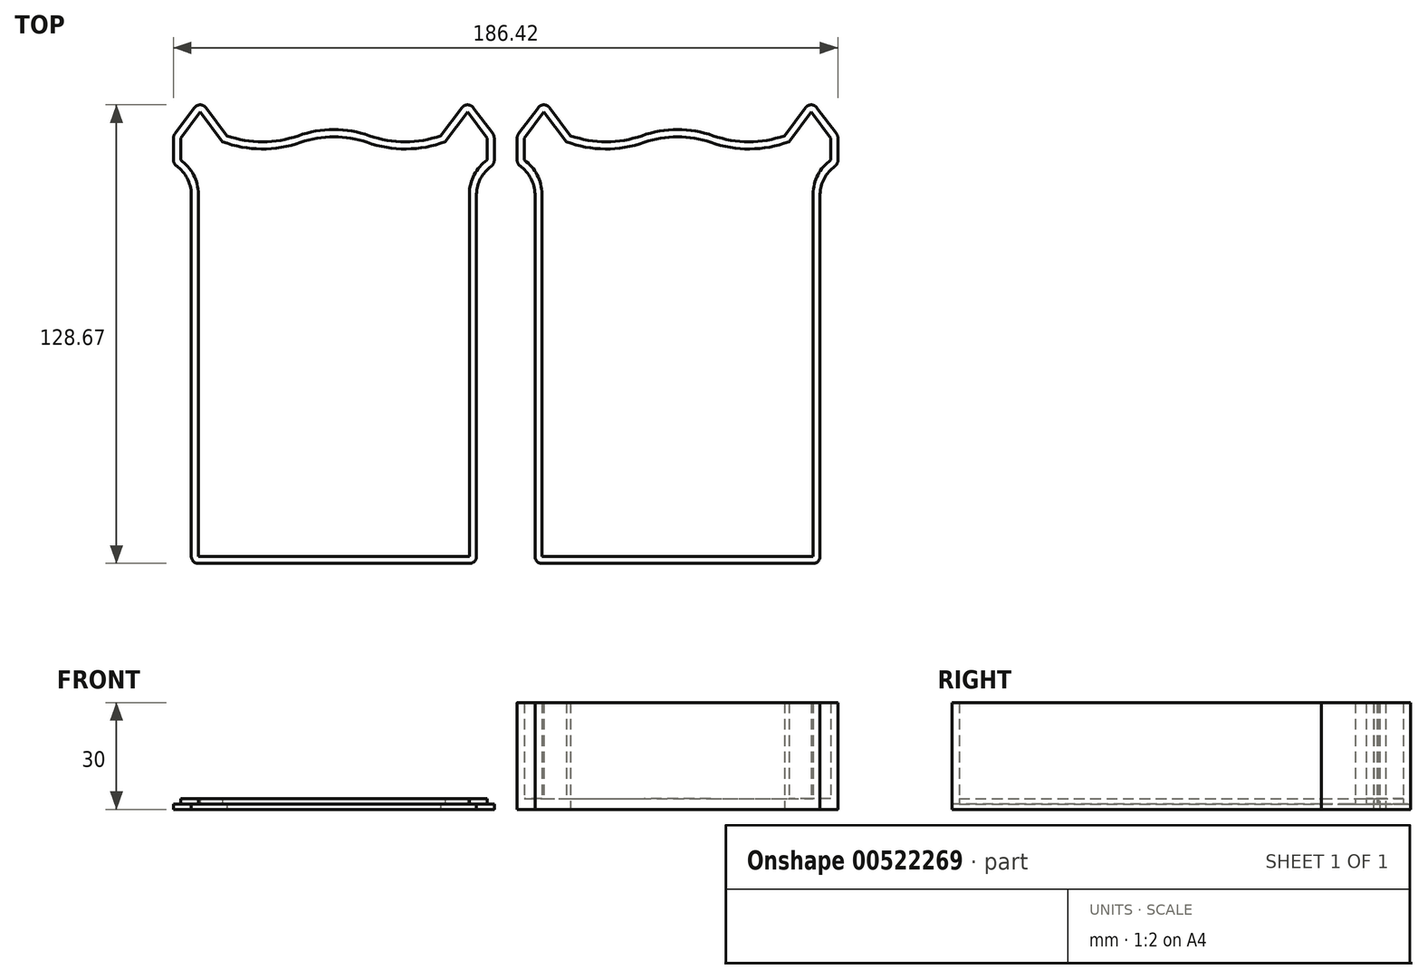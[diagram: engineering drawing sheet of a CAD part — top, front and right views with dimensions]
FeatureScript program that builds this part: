
annotation { "Feature Type Name" : "Feature", "Feature Type Description" : "" }
export const myFeature = defineFeature(function(context is Context, id is Id, definition is map)
    precondition{}
    {
        {
            var Q0;
            Q0=qCreatedBy(makeId("Top.planeOp"),FACE);
            var sketch = newSketch(context, id + "F0", { "sketchPlane" : qUnion([Q0])});
            skLineSegment(sketch, "E0", {"start": v(2, 0) * mm, "end": v(78, 0) * mm});
            skLineSegment(sketch, "E1", {"start": v(0, 2) * mm, "end": v(0, 103.64) * mm});
            skLineSegment(sketch, "E2", {"start": v(80, 103.6) * mm, "end": v(80, 2) * mm});
            skPoint(sketch, "E3", {"position": v(80, 110) * mm});
            skPoint(sketch, "E4", {"position": v(40, 120) * mm});
            skPoint(sketch, "E5", {"position": v(10, 120) * mm});
            skPoint(sketch, "E6", {"position": v(30, 120) * mm});
            skPoint(sketch, "E7", {"position": v(50, 120) * mm});
            skArc(sketch, "E8", {"start": v(10, 120) * mm, "mid": v(20, 118.28) * mm, "end": v(30, 120) * mm});
            skArc(sketch, "E9", {"start": v(50, 120) * mm, "mid": v(40, 121.72) * mm, "end": v(30, 120) * mm});
            skArc(sketch, "E10", {"start": v(50, 120) * mm, "mid": v(60, 118.28) * mm, "end": v(70, 120) * mm});
            skPoint(sketch, "E11", {"position": v(20, 130.8) * mm});
            skPoint(sketch, "E11.positionSnap0", {"position": v(20, 118.28) * mm});
            skLineSegment(sketch, "E12", {"start": v(-5, 113.15) * mm, "end": v(-5, 119.33) * mm});
            skLineSegment(sketch, "E13", {"start": v(85, 113.09) * mm, "end": v(85, 119.33) * mm});
            skLineSegment(sketch, "E14", {"start": v(-4.6, 120.53) * mm, "end": v(0.9, 127.87) * mm});
            skLineSegment(sketch, "E15", {"start": v(4.1, 127.87) * mm, "end": v(10, 120) * mm});
            skPoint(sketch, "E16", {"position": v(-5, 120) * mm});
            skPoint(sketch, "E17", {"position": v(2.5, 120) * mm});
            skPoint(sketch, "E18.visualSharp", {"position": v(2.5, 130) * mm});
            skArc(sketch, "E18.filletArc", {"start": v(4.1, 127.87) * mm, "mid": v(2.5, 128.67) * mm, "end": v(0.9, 127.87) * mm});
            skPoint(sketch, "E19.endSnap0", {"position": v(40, 110) * mm});
            skLineSegment(sketch, "E20.MirrorCS", {"start": v(75.9, 127.87) * mm, "end": v(70, 120) * mm});
            skLineSegment(sketch, "E21.MirrorCS", {"start": v(84.6, 120.53) * mm, "end": v(79.1, 127.87) * mm});
            skArc(sketch, "E22.MirrorCS", {"start": v(75.9, 127.87) * mm, "mid": v(77.5, 128.67) * mm, "end": v(79.1, 127.87) * mm});
            skPoint(sketch, "E23.visualSharp", {"position": v(85, 110) * mm});
            skPoint(sketch, "E24.visualSharp", {"position": v(-5, 110) * mm});
            skArc(sketch, "E25", {"start": v(0, 103.64) * mm, "mid": v(-1.16, 108.08) * mm, "end": v(-4.17, 111.53) * mm});
            skPoint(sketch, "E26.orphan", {"position": v(0, 110) * mm});
            skPoint(sketch, "E27.visualSharp", {"position": v(-5, 112.07) * mm});
            skArc(sketch, "E27.filletArc", {"start": v(-5, 113.15) * mm, "mid": v(-4.78, 112.24) * mm, "end": v(-4.17, 111.53) * mm});
            skArc(sketch, "E28.filletArc", {"start": v(-4.6, 120.53) * mm, "mid": v(-4.9, 119.97) * mm, "end": v(-5, 119.33) * mm});
            skArc(sketch, "E29.MirrorCS", {"start": v(80, 103.6) * mm, "mid": v(81.16, 108.02) * mm, "end": v(84.17, 111.46) * mm});
            skArc(sketch, "E30.MirrorCS", {"start": v(85, 113.09) * mm, "mid": v(84.78, 112.17) * mm, "end": v(84.17, 111.46) * mm});
            skPoint(sketch, "E31.visualSharp", {"position": v(85, 120) * mm});
            skArc(sketch, "E31.filletArc", {"start": v(85, 119.33) * mm, "mid": v(84.9, 119.97) * mm, "end": v(84.6, 120.53) * mm});
            skArc(sketch, "E32.0", {"start": v(8.76, 118.32) * mm, "mid": v(19.7, 116.29) * mm, "end": v(30.67, 118.11) * mm});
            skLineSegment(sketch, "E32.1", {"start": v(2.5, 126.67) * mm, "end": v(8.76, 118.32) * mm});
            skLineSegment(sketch, "E32.2", {"start": v(2, 2) * mm, "end": v(2, 103.67) * mm});
            skArc(sketch, "E32.3", {"start": v(2, 103.67) * mm, "mid": v(0.62, 109) * mm, "end": v(-3, 113.15) * mm});
            skLineSegment(sketch, "E32.4", {"start": v(-3, 113.15) * mm, "end": v(-3, 119.33) * mm});
            skLineSegment(sketch, "E32.5", {"start": v(-3, 119.33) * mm, "end": v(2.5, 126.67) * mm});
            skArc(sketch, "E33.MirrorCS", {"start": v(71.24, 118.32) * mm, "mid": v(60.3, 116.29) * mm, "end": v(49.33, 118.11) * mm});
            skLineSegment(sketch, "E34.MirrorCS", {"start": v(77.5, 126.67) * mm, "end": v(71.24, 118.32) * mm});
            skLineSegment(sketch, "E35.MirrorCS", {"start": v(83, 119.33) * mm, "end": v(77.5, 126.67) * mm});
            skLineSegment(sketch, "E36.MirrorCS", {"start": v(83, 113.15) * mm, "end": v(83, 119.33) * mm});
            skArc(sketch, "E37.MirrorCS", {"start": v(78, 103.67) * mm, "mid": v(79.38, 109) * mm, "end": v(83, 113.15) * mm});
            skArc(sketch, "E38.0", {"start": v(49.33, 118.11) * mm, "mid": v(40, 119.72) * mm, "end": v(30.67, 118.11) * mm});
            skLineSegment(sketch, "E39.0", {"start": v(2, 2) * mm, "end": v(78, 2) * mm});
            skLineSegment(sketch, "E39.1", {"start": v(78, 103.6) * mm, "end": v(78, 2) * mm});
            skLineSegment(sketch, "E40", {"start": v(78, 103.6) * mm, "end": v(78, 103.67) * mm});
            skPoint(sketch, "E41", {"position": v(0, 0) * mm});
            skPoint(sketch, "E42", {"position": v(2, 2) * mm});
            skArc(sketch, "E43.filletArc", {"start": v(0, 2) * mm, "mid": v(0.59, 0.59) * mm, "end": v(2, 0) * mm});
            skPoint(sketch, "E44.visualSharp", {"position": v(80, 0) * mm});
            skArc(sketch, "E44.filletArc", {"start": v(78, 0) * mm, "mid": v(79.41, 0.59) * mm, "end": v(80, 2) * mm});
            skSolve(sketch);
        }
        {
            var Q0;
            Q0=makeQuery(id+"F0.imprint","IMPRINT",FACE,{"disambiguationData":[TD([[makeQuery(id+"F0.imprint","IMPRINT",EDGE,{"derivedFrom":sQuery(id+"F0.wireOp",EDGE,"E0")}),1.0]])]});
            extrude(context, id + "F1", {"entities" : qUnion([Q0]), "depth" : 30 * mm, "offsetDistance" : 25 * mm});
        }
        {
            var Q0;
            Q0=makeQuery(id+"F0.imprint","IMPRINT",FACE,{"disambiguationData":[TD([[makeQuery(id+"F0.imprint","IMPRINT",EDGE,{"derivedFrom":sQuery(id+"F0.wireOp",EDGE,"E32.0")}),-1.0]])]});
            extrude(context, id + "F2", {"entities" : qUnion([Q0]), "operationType" : NewBodyOperationType.ADD, "depth" : 3 * mm, "offsetDistance" : 25 * mm});
        }
        {
            var Q0;
            Q0=qCreatedBy(makeId("Top.planeOp"),FACE);
            var sketch = newSketch(context, id + "F3", { "sketchPlane" : qUnion([Q0])});
            skLineSegment(sketch, "E45", {"start": v(-94.42, 0) * mm, "end": v(-18.42, 0) * mm});
            skLineSegment(sketch, "E46", {"start": v(-96.42, 2) * mm, "end": v(-96.42, 103.64) * mm});
            skLineSegment(sketch, "E47", {"start": v(-16.42, 103.6) * mm, "end": v(-16.42, 2) * mm});
            skPoint(sketch, "E48", {"position": v(-16.42, 110) * mm});
            skPoint(sketch, "E49", {"position": v(-56.42, 120) * mm});
            skPoint(sketch, "E50", {"position": v(-86.42, 120) * mm});
            skPoint(sketch, "E51", {"position": v(-66.42, 120) * mm});
            skPoint(sketch, "E52", {"position": v(-46.42, 120) * mm});
            skArc(sketch, "E53", {"start": v(-86.42, 120) * mm, "mid": v(-76.42, 118.28) * mm, "end": v(-66.42, 120) * mm});
            skArc(sketch, "E54", {"start": v(-46.42, 120) * mm, "mid": v(-56.42, 121.72) * mm, "end": v(-66.42, 120) * mm});
            skArc(sketch, "E55", {"start": v(-46.42, 120) * mm, "mid": v(-36.42, 118.28) * mm, "end": v(-26.42, 120) * mm});
            skPoint(sketch, "E56", {"position": v(-76.42, 130.8) * mm});
            skPoint(sketch, "E56.positionSnap0", {"position": v(-76.42, 118.28) * mm});
            skLineSegment(sketch, "E57", {"start": v(-101.42, 113.15) * mm, "end": v(-101.42, 119.33) * mm});
            skLineSegment(sketch, "E58", {"start": v(-11.42, 113.09) * mm, "end": v(-11.42, 119.33) * mm});
            skLineSegment(sketch, "E59", {"start": v(-101.02, 120.53) * mm, "end": v(-95.52, 127.87) * mm});
            skLineSegment(sketch, "E60", {"start": v(-92.32, 127.87) * mm, "end": v(-86.42, 120) * mm});
            skPoint(sketch, "E61", {"position": v(-101.42, 120) * mm});
            skPoint(sketch, "E62", {"position": v(-93.92, 120) * mm});
            skPoint(sketch, "E63.visualSharp", {"position": v(-93.92, 130) * mm});
            skArc(sketch, "E63.filletArc", {"start": v(-92.32, 127.87) * mm, "mid": v(-93.92, 128.67) * mm, "end": v(-95.52, 127.87) * mm});
            skPoint(sketch, "E64.endSnap0", {"position": v(-56.42, 110) * mm});
            skLineSegment(sketch, "E65.MirrorCS", {"start": v(-20.52, 127.87) * mm, "end": v(-26.42, 120) * mm});
            skLineSegment(sketch, "E66.MirrorCS", {"start": v(-11.82, 120.53) * mm, "end": v(-17.32, 127.87) * mm});
            skArc(sketch, "E67.MirrorCS", {"start": v(-20.52, 127.87) * mm, "mid": v(-18.92, 128.67) * mm, "end": v(-17.32, 127.87) * mm});
            skPoint(sketch, "E68.visualSharp", {"position": v(-11.42, 110) * mm});
            skPoint(sketch, "E69.visualSharp", {"position": v(-101.42, 110) * mm});
            skArc(sketch, "E70", {"start": v(-96.42, 103.64) * mm, "mid": v(-97.57, 108.08) * mm, "end": v(-100.59, 111.53) * mm});
            skPoint(sketch, "E71.orphan", {"position": v(-96.42, 110) * mm});
            skPoint(sketch, "E72.visualSharp", {"position": v(-101.42, 112.07) * mm});
            skArc(sketch, "E72.filletArc", {"start": v(-101.42, 113.15) * mm, "mid": v(-101.2, 112.24) * mm, "end": v(-100.59, 111.53) * mm});
            skArc(sketch, "E73.filletArc", {"start": v(-101.02, 120.53) * mm, "mid": v(-101.32, 119.97) * mm, "end": v(-101.42, 119.33) * mm});
            skArc(sketch, "E74.MirrorCS", {"start": v(-16.42, 103.6) * mm, "mid": v(-15.26, 108.02) * mm, "end": v(-12.25, 111.46) * mm});
            skArc(sketch, "E75.MirrorCS", {"start": v(-11.42, 113.09) * mm, "mid": v(-11.64, 112.17) * mm, "end": v(-12.25, 111.46) * mm});
            skPoint(sketch, "E76.visualSharp", {"position": v(-11.42, 120) * mm});
            skArc(sketch, "E76.filletArc", {"start": v(-11.42, 119.33) * mm, "mid": v(-11.52, 119.97) * mm, "end": v(-11.82, 120.53) * mm});
            skArc(sketch, "E77.0", {"start": v(-87.66, 118.32) * mm, "mid": v(-76.73, 116.29) * mm, "end": v(-65.75, 118.11) * mm});
            skLineSegment(sketch, "E77.1", {"start": v(-93.92, 126.67) * mm, "end": v(-87.66, 118.32) * mm});
            skLineSegment(sketch, "E77.2", {"start": v(-94.42, 2) * mm, "end": v(-94.42, 103.67) * mm});
            skArc(sketch, "E77.3", {"start": v(-94.42, 103.67) * mm, "mid": v(-95.8, 109) * mm, "end": v(-99.42, 113.15) * mm});
            skLineSegment(sketch, "E77.4", {"start": v(-99.42, 113.15) * mm, "end": v(-99.42, 119.33) * mm});
            skLineSegment(sketch, "E77.5", {"start": v(-99.42, 119.33) * mm, "end": v(-93.92, 126.67) * mm});
            skArc(sketch, "E78.MirrorCS", {"start": v(-25.18, 118.32) * mm, "mid": v(-36.11, 116.29) * mm, "end": v(-47.09, 118.11) * mm});
            skLineSegment(sketch, "E79.MirrorCS", {"start": v(-18.92, 126.67) * mm, "end": v(-25.18, 118.32) * mm});
            skLineSegment(sketch, "E80.MirrorCS", {"start": v(-13.42, 119.33) * mm, "end": v(-18.92, 126.67) * mm});
            skLineSegment(sketch, "E81.MirrorCS", {"start": v(-13.42, 113.15) * mm, "end": v(-13.42, 119.33) * mm});
            skArc(sketch, "E82.MirrorCS", {"start": v(-18.42, 103.67) * mm, "mid": v(-17.04, 109) * mm, "end": v(-13.42, 113.15) * mm});
            skArc(sketch, "E83.0", {"start": v(-47.09, 118.11) * mm, "mid": v(-56.42, 119.72) * mm, "end": v(-65.75, 118.11) * mm});
            skLineSegment(sketch, "E84.0", {"start": v(-94.42, 2) * mm, "end": v(-18.42, 2) * mm});
            skLineSegment(sketch, "E84.1", {"start": v(-18.42, 103.6) * mm, "end": v(-18.42, 2) * mm});
            skLineSegment(sketch, "E85", {"start": v(-18.42, 103.6) * mm, "end": v(-18.42, 103.67) * mm});
            skPoint(sketch, "E86", {"position": v(-96.42, 0) * mm});
            skPoint(sketch, "E87", {"position": v(-94.42, 2) * mm});
            skArc(sketch, "E88.filletArc", {"start": v(-96.42, 2) * mm, "mid": v(-95.83, 0.59) * mm, "end": v(-94.42, 0) * mm});
            skPoint(sketch, "E89.visualSharp", {"position": v(-16.42, 0) * mm});
            skArc(sketch, "E89.filletArc", {"start": v(-18.42, 0) * mm, "mid": v(-17, 0.59) * mm, "end": v(-16.42, 2) * mm});
            skSolve(sketch);
        }
        {
            var Q0;
            Q0=makeQuery(id+"F3.imprint","IMPRINT",FACE,{"disambiguationData":[TD([[makeQuery(id+"F3.imprint","IMPRINT",EDGE,{"derivedFrom":sQuery(id+"F3.wireOp",EDGE,"E77.0")}),-1.0]])]});
            extrude(context, id + "F4", {"entities" : qUnion([Q0]), "depth" : 3 * mm, "offsetDistance" : 25 * mm});
        }
        {
            var Q0;
            Q0 = qSketchRegion(id + "F3", true);
            extrude(context, id + "F5", {"entities" : qUnion([Q0]), "operationType" : NewBodyOperationType.ADD, "depth" : 1.5 * mm, "offsetDistance" : 25 * mm});
        }
    });
